# Revit family: Nebula 01
name_source: partatom
category: Lighting Fixtures
units: mm (PartAtom-declared; Revit-internal decimal feet)

## family parameters
Always vertical = Yes
Cut with Voids When Loaded = No
Host = Ceiling
Light Source = Yes
OmniClass Number = 23.80.70.11
OmniClass Title = Luminaries for Internal Lighting
Part Type = Normal
Room Calculation Point = No
Round Connector Dimension = Use Diameter
Shared = No

## types (4) — shared parameters
Color Filter = 16777215
Default Elevation = 0' - 0"
Diffuser = Matte White Acrylic
Dimming Lamp Color Temperature Shift = <None>
Lamp = LED Array
Light Source Symbol Size = 2' - 0"
Manufacturer = Oxygen Lighting and Fans
Model = 3-680-xx Nebula Pendant
References = Ref. 3 = 120 V / Ref. 37 = 277 V
URL = www.oxygenlighting.com
Voltage Input = 120 V or 277 V - 50/60 Hz
Wattage Comments = 6 W at 120 V

## per-type parameters (varying)
| type | Metal Finish | Voltage |
| 3-680-15 / Black - Matte White Acrylic | 15 - Black | 120 V |
| 3-680-40 / Aged Brass - Matte White Acrylic | 40 - Aged Brass | 120 V |
| 36-680-15 / Black - Matte White Acrylic | 15 - Black | 277 V |
| 36-680-40 / Aged Brass - Matte White Acrylic | 40 - Aged Brass | 277 V |

## geometry (parser evidence)
native form markers: Sweep x6
no freeform markers — native parametric forms only
